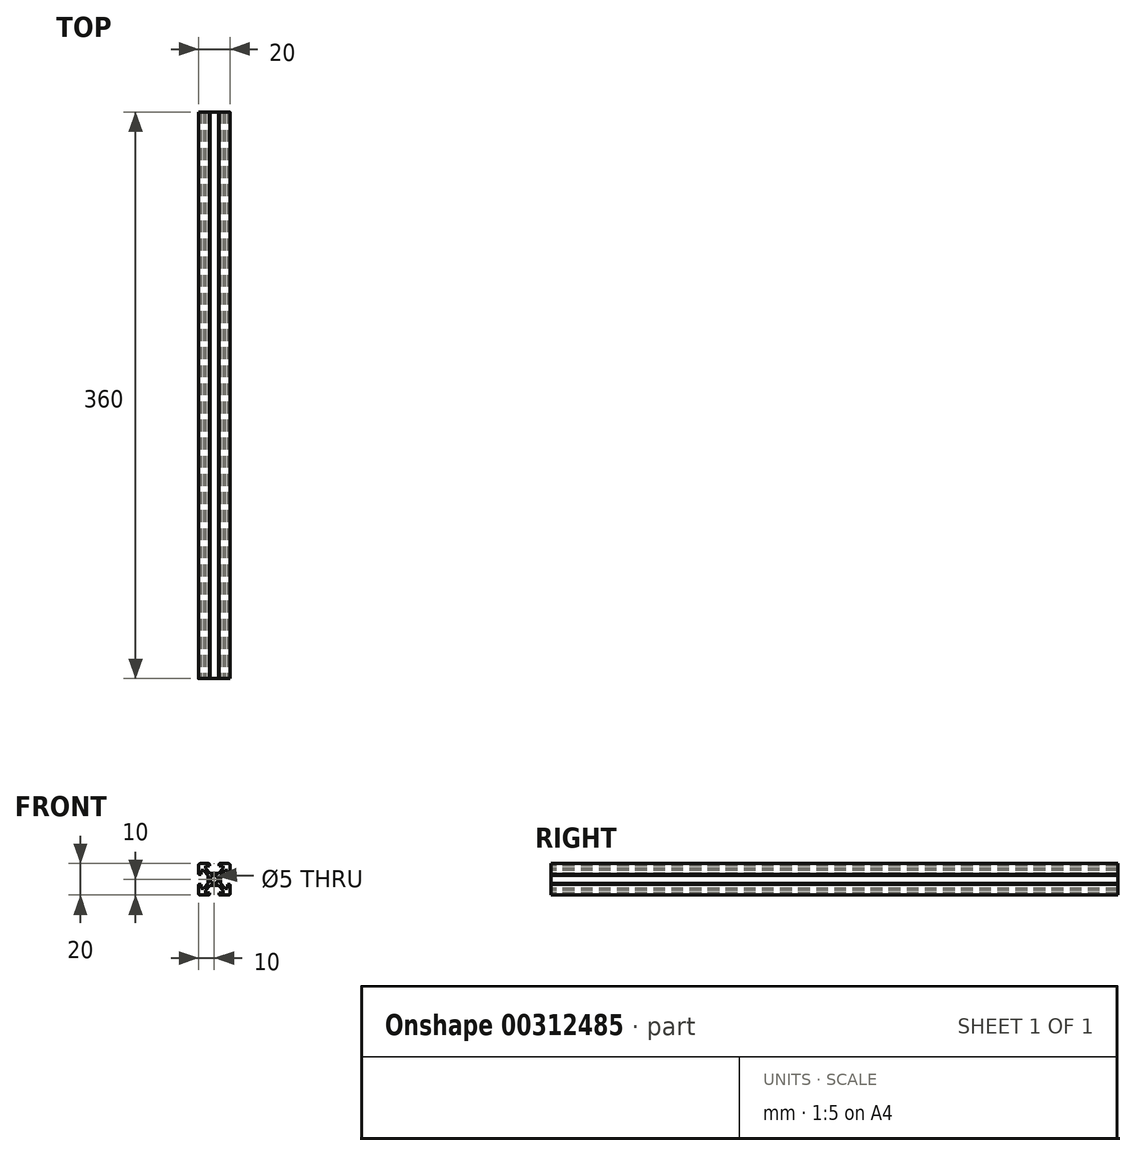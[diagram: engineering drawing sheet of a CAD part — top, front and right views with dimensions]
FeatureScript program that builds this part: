
annotation { "Feature Type Name" : "Feature", "Feature Type Description" : "" }
export const myFeature = defineFeature(function(context is Context, id is Id, definition is map)
    precondition{}
    {
        {
            var Q0;
            Q0=qCreatedBy(makeId("Front.planeOp"),FACE);
            var sketch = newSketch(context, id + "F0", { "sketchPlane" : qUnion([Q0])});
            skLineSegment(sketch, "E0.top", {"start": v(-3.6, 10) * mm, "end": v(-9, 10) * mm});
            skLineSegment(sketch, "E0.right", {"start": v(-10, 3.6) * mm, "end": v(-10, 9) * mm});
            skLineSegment(sketch, "E1", {"start": v(-3.1, 9.5) * mm, "end": v(-3.1, 8.46) * mm});
            skLineSegment(sketch, "E2", {"start": v(-3.1, 8.46) * mm, "end": v(-5.63, 8.46) * mm});
            skLineSegment(sketch, "E3", {"start": v(-5.63, 8.46) * mm, "end": v(-5.63, 6.92) * mm});
            skLineSegment(sketch, "E4", {"start": v(-5.63, 6.92) * mm, "end": v(-2.61, 3.9) * mm});
            skPoint(sketch, "E5.visualSharp", {"position": v(-3.1, 10) * mm});
            skArc(sketch, "E5.filletArc", {"start": v(-3.1, 9.5) * mm, "mid": v(-3.25, 9.85) * mm, "end": v(-3.6, 10) * mm});
            skLineSegment(sketch, "E6.MirrorCS", {"start": v(-6.92, 5.63) * mm, "end": v(-3.9, 2.61) * mm});
            skLineSegment(sketch, "E7.MirrorCS", {"start": v(-8.46, 3.1) * mm, "end": v(-8.46, 5.63) * mm});
            skLineSegment(sketch, "E8.MirrorCS", {"start": v(-9.5, 3.1) * mm, "end": v(-8.46, 3.1) * mm});
            skArc(sketch, "E9.MirrorCS", {"start": v(-9.5, 3.1) * mm, "mid": v(-9.85, 3.25) * mm, "end": v(-10, 3.6) * mm});
            skPoint(sketch, "E10.visualSharp", {"position": v(-10, 10) * mm});
            skArc(sketch, "E10.filletArc", {"start": v(-9, 10) * mm, "mid": v(-9.7, 9.7) * mm, "end": v(-10, 9) * mm});
            skLineSegment(sketch, "E11.MirrorCS", {"start": v(6.92, 5.63) * mm, "end": v(3.9, 2.61) * mm});
            skLineSegment(sketch, "E12.MirrorCS", {"start": v(8.46, 3.1) * mm, "end": v(8.46, 5.63) * mm});
            skLineSegment(sketch, "E13.MirrorCS", {"start": v(9.5, 3.1) * mm, "end": v(8.46, 3.1) * mm});
            skArc(sketch, "E14.MirrorCS", {"start": v(9.5, 3.1) * mm, "mid": v(9.85, 3.25) * mm, "end": v(10, 3.6) * mm});
            skLineSegment(sketch, "E15.MirrorCS", {"start": v(10, 3.6) * mm, "end": v(10, 9) * mm});
            skArc(sketch, "E16.MirrorCS", {"start": v(9, 10) * mm, "mid": v(9.7, 9.7) * mm, "end": v(10, 9) * mm});
            skLineSegment(sketch, "E17.MirrorCS", {"start": v(3.6, 10) * mm, "end": v(9, 10) * mm});
            skArc(sketch, "E18.MirrorCS", {"start": v(3.1, 9.5) * mm, "mid": v(3.25, 9.85) * mm, "end": v(3.6, 10) * mm});
            skLineSegment(sketch, "E19.MirrorCS", {"start": v(3.1, 9.5) * mm, "end": v(3.1, 8.46) * mm});
            skLineSegment(sketch, "E20.MirrorCS", {"start": v(3.1, 8.46) * mm, "end": v(5.63, 8.46) * mm});
            skLineSegment(sketch, "E21.MirrorCS", {"start": v(5.63, 6.92) * mm, "end": v(2.61, 3.9) * mm});
            skPoint(sketch, "E22.orphan", {"position": v(-6.92, 5.63) * mm});
            skPoint(sketch, "E23.MirrorCS.end.orphan", {"position": v(-10, 5.63) * mm});
            skLineSegment(sketch, "E24", {"start": v(-8.46, 5.63) * mm, "end": v(-6.92, 5.63) * mm});
            skPoint(sketch, "E25.MirrorCS.start.orphan", {"position": v(5.63, 6.92) * mm});
            skPoint(sketch, "E26.orphan", {"position": v(6.92, 5.63) * mm});
            skPoint(sketch, "E27.MirrorCS.end.orphan", {"position": v(10, 5.63) * mm});
            skLineSegment(sketch, "E28.MirrorCS", {"start": v(5.63, 8.46) * mm, "end": v(5.63, 6.92) * mm});
            skLineSegment(sketch, "E29.MirrorCS", {"start": v(8.46, 5.63) * mm, "end": v(6.92, 5.63) * mm});
            skLineSegment(sketch, "E30.MirrorCS", {"start": v(6.92, -5.63) * mm, "end": v(3.9, -2.61) * mm});
            skLineSegment(sketch, "E31.MirrorCS", {"start": v(5.63, -6.92) * mm, "end": v(2.61, -3.9) * mm});
            skLineSegment(sketch, "E32.MirrorCS", {"start": v(-5.63, -6.92) * mm, "end": v(-2.61, -3.9) * mm});
            skLineSegment(sketch, "E33.MirrorCS", {"start": v(-6.92, -5.63) * mm, "end": v(-3.9, -2.61) * mm});
            skLineSegment(sketch, "E34.MirrorCS", {"start": v(-8.46, -3.1) * mm, "end": v(-8.46, -5.63) * mm});
            skLineSegment(sketch, "E35.MirrorCS", {"start": v(-9.5, -3.1) * mm, "end": v(-8.46, -3.1) * mm});
            skArc(sketch, "E36.MirrorCS", {"start": v(-9.5, -3.1) * mm, "mid": v(-9.85, -3.25) * mm, "end": v(-10, -3.6) * mm});
            skLineSegment(sketch, "E37.MirrorCS", {"start": v(-10, -3.6) * mm, "end": v(-10, -9) * mm});
            skLineSegment(sketch, "E38.MirrorCS", {"start": v(8.46, -5.63) * mm, "end": v(6.92, -5.63) * mm});
            skLineSegment(sketch, "E39.MirrorCS", {"start": v(8.46, -3.1) * mm, "end": v(8.46, -5.63) * mm});
            skLineSegment(sketch, "E40.MirrorCS", {"start": v(9.5, -3.1) * mm, "end": v(8.46, -3.1) * mm});
            skArc(sketch, "E41.MirrorCS", {"start": v(9.5, -3.1) * mm, "mid": v(9.85, -3.25) * mm, "end": v(10, -3.6) * mm});
            skLineSegment(sketch, "E42.MirrorCS", {"start": v(10, -3.6) * mm, "end": v(10, -9) * mm});
            skLineSegment(sketch, "E43.MirrorCS", {"start": v(-8.46, -5.63) * mm, "end": v(-6.92, -5.63) * mm});
            skLineSegment(sketch, "E44.MirrorCS", {"start": v(-5.63, -8.46) * mm, "end": v(-5.63, -6.92) * mm});
            skLineSegment(sketch, "E45.MirrorCS", {"start": v(-3.1, -8.46) * mm, "end": v(-5.63, -8.46) * mm});
            skLineSegment(sketch, "E46.MirrorCS", {"start": v(-3.1, -9.5) * mm, "end": v(-3.1, -8.46) * mm});
            skLineSegment(sketch, "E47.MirrorCS", {"start": v(-3.6, -10) * mm, "end": v(-9, -10) * mm});
            skLineSegment(sketch, "E48.MirrorCS", {"start": v(3.1, -9.5) * mm, "end": v(3.1, -8.46) * mm});
            skArc(sketch, "E49.MirrorCS", {"start": v(3.1, -9.5) * mm, "mid": v(3.25, -9.85) * mm, "end": v(3.6, -10) * mm});
            skLineSegment(sketch, "E50.MirrorCS", {"start": v(3.6, -10) * mm, "end": v(9, -10) * mm});
            skLineSegment(sketch, "E51.MirrorCS", {"start": v(3.1, -8.46) * mm, "end": v(5.63, -8.46) * mm});
            skLineSegment(sketch, "E52.MirrorCS", {"start": v(5.63, -8.46) * mm, "end": v(5.63, -6.92) * mm});
            skArc(sketch, "E53.MirrorCS", {"start": v(9, -10) * mm, "mid": v(9.7, -9.7) * mm, "end": v(10, -9) * mm});
            skArc(sketch, "E54.MirrorCS", {"start": v(-9, -10) * mm, "mid": v(-9.7, -9.7) * mm, "end": v(-10, -9) * mm});
            skArc(sketch, "E55.MirrorCS", {"start": v(-3.1, -9.5) * mm, "mid": v(-3.25, -9.85) * mm, "end": v(-3.6, -10) * mm});
            skPoint(sketch, "E56.MirrorCS.start.orphan", {"position": v(-3.9, 2.61) * mm});
            skPoint(sketch, "E57.MirrorCS.start.orphan", {"position": v(-3.9, -2.61) * mm});
            skPoint(sketch, "E58.MirrorCS.start.orphan", {"position": v(2.61, 3.9) * mm});
            skPoint(sketch, "E59.MirrorCS.start.orphan", {"position": v(3.9, 2.61) * mm});
            skPoint(sketch, "E60.MirrorCS.start.orphan", {"position": v(3.9, -2.61) * mm});
            skPoint(sketch, "E61.MirrorCS.start.orphan", {"position": v(2.61, -3.9) * mm});
            skPoint(sketch, "E62.MirrorCS.start.orphan", {"position": v(-2.61, -3.9) * mm});
            skLineSegment(sketch, "E63", {"start": v(-3.9, 2.61) * mm, "end": v(-3.9, -2.61) * mm});
            skLineSegment(sketch, "E64", {"start": v(-2.61, 3.9) * mm, "end": v(2.61, 3.9) * mm});
            skLineSegment(sketch, "E65", {"start": v(3.9, 2.61) * mm, "end": v(3.9, -2.61) * mm});
            skLineSegment(sketch, "E66", {"start": v(-2.61, -3.9) * mm, "end": v(2.61, -3.9) * mm});
            skCircle(sketch, "E67", {"center": v(0, 0) * mm, "radius": 2.5 * mm});
            skSolve(sketch);
        }
        {
            var Q0;
            Q0 = qSketchRegion(id + "F0", true);
            extrude(context, id + "F1", {"entities" : qUnion([Q0]), "oppositeDirection" : true, "depth" : 360 * mm});
        }
    });
